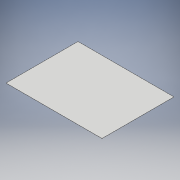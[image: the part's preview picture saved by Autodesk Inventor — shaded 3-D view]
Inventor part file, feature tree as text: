
AUTODESK INVENTOR PART (.ipt)
format: ipt  version: 2017 (Build 210142000, 142)  size: 93,696 bytes
history: native  units: mm
features: sheet_metal_op x1, sketch x1, other x1
ambient origin geometry x8: Origin, YZ Plane, XZ Plane, XY Plane, X Axis, Y Axis, Z Axis, Center Point
bodies: Solid1 (feature_tree)
feature tree (3):
  sheet_metal_op  "Face1"
  sketch  "Sketch1"  dims[d0=400.0mm d1=300.0mm d2=0.5mm]
  other  "Plate1"
